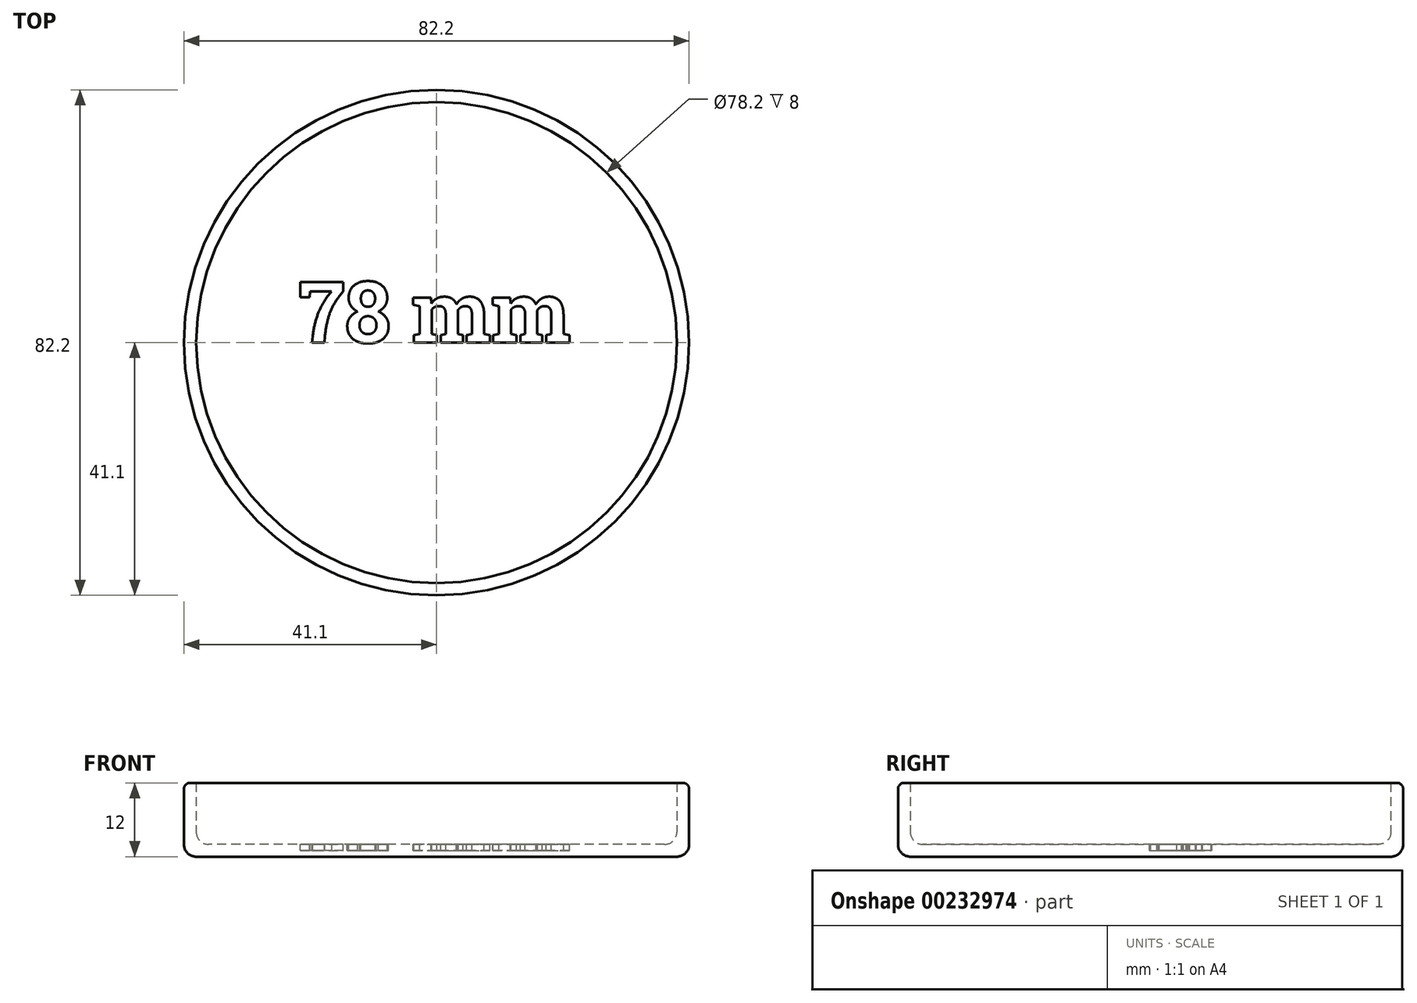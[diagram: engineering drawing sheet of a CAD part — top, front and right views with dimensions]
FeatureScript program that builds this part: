
annotation { "Feature Type Name" : "Feature", "Feature Type Description" : "" }
export const myFeature = defineFeature(function(context is Context, id is Id, definition is map)
    precondition{}
    {
        {
            assignVariable(context, id + "F0", {"name" : "Kappen_staerke", "anyValue" : 2 * mm});
        }
        {
            assignVariable(context, id + "F1", {"name" : "Kappen_hoehe", "anyValue" : 10 * mm});
        }
        {
            var Q0;
            Q0=qCreatedBy(makeId("Top.planeOp"),FACE);
            var sketch = newSketch(context, id + "F2", { "sketchPlane" : qUnion([Q0])});
            skCircle(sketch, "E0", {"center": v(0, 0) * mm, "radius": 39.1 * mm});
            skSolve(sketch);
        }
        {
            var Q0;
            Q0=makeQuery(id+"F2.imprint","IMPRINT",FACE,{"disambiguationData":[TD([[makeQuery(id+"F2.imprint","IMPRINT",EDGE,{"derivedFrom":sQuery(id+"F2.wireOp",EDGE,"E0")}),1.0]])]});
            extrude(context, id + "F3", {"entities" : qUnion([Q0]), "depth" : getVariable(context, 'Kappen_hoehe')});
        }
        {
            var Q0;
            Q0=makeQuery(id+"F3.opExtrude","CAP_FACE",FACE,{"disambiguationData":[OSD([sQuery(id+"F2.wireOp",EDGE,"E0")])],"isStart":false});
            shell(context, id + "F4", {"entities" : qUnion([Q0]), "thickness" : getVariable(context, 'Kappen_staerke'), "oppositeDirection" : true});
        }
        {
            var Q0;
            Q0=makeQuery(id+"F3.opExtrude","CAP_EDGE",EDGE,{"disambiguationData":[OSD([sQuery(id+"F2.wireOp",EDGE,"E0")])],"isStart":true});
            fillet(context, id + "F5", {"entities" : qUnion([Q0]), "radius" : 2 * mm, "tangentPropagation" : true, "allowEdgeOverflow" : false});
        }
        {
            var Q0;
            {var subQ0=sQuery(id+"F2.wireOp",EDGE,"E0");Q0=makeQuery(id+"F4.opShell","OFFSET_EDGE",EDGE,{"disambiguationData":[OSD([subQ0]),TDD([makeQuery(id+"F3.opExtrude","CAP_EDGE",EDGE,{"disambiguationData":[OSD([subQ0])],"isStart":true})])]});}
            fillet(context, id + "F6", {"entities" : qUnion([Q0]), "radius" : 2 * mm, "tangentPropagation" : true, "allowEdgeOverflow" : false});
        }
        {
            var Q0;
            Q0=makeQuery(id+"F3.opExtrude","CAP_EDGE",EDGE,{"disambiguationData":[OSD([sQuery(id+"F2.wireOp",EDGE,"E0")])],"isStart":false});
            fillet(context, id + "F7", {"entities" : qUnion([Q0]), "radius" : 1 * mm, "tangentPropagation" : true, "allowEdgeOverflow" : false});
        }
        {
            var Q0;
            {var subQ0=sQuery(id+"F2.wireOp",EDGE,"E0");Q0=makeQuery(id+"F4.opShell","OFFSET_FACE",FACE,{"disambiguationData":[OSD([subQ0]),TDD([makeQuery(id+"F3.opExtrude","CAP_FACE",FACE,{"disambiguationData":[OSD([subQ0])],"isStart":true})])]});}
            var sketch = newSketch(context, id + "F8", { "sketchPlane" : qUnion([Q0])});
            skText(sketch, "E1", { "text": "78 mm ", "fontName": "RobotoSlab-Bold.ttf"});
            const initialGuessF8  = {"E1": [-0.02248, 0, 1, 0, 0.01], "E1": [-0.02248, 0, 1, 0, 0.01]};
            skSetInitialGuess(sketch, initialGuessF8);
            skSolve(sketch);
        }
        {
            var Q0;
            Q0 = qSketchRegion(id + "F8", true);
            extrude(context, id + "F9", {"entities" : qUnion([Q0]), "operationType" : NewBodyOperationType.REMOVE, "oppositeDirection" : true, "depth" : 1 * mm});
        }
    });
